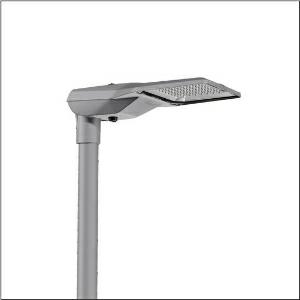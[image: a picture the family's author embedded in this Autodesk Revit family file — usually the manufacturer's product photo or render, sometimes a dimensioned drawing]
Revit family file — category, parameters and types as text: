
# Revit family: streetlight_sl_21_midi___pc-r_5xe3g33t08mb_dbe8
name_source: partatom
category: Lighting Fixtures
units: mm (PartAtom-declared; Revit-internal decimal feet)

## family parameters
Cut with Voids When Loaded = No
Host = Face
Light Source = No
Part Type = Normal
Room Calculation Point = No
Round Connector Dimension = Use Diameter
Shared = No

## types (1)
- --- (1 x LED, 17390 lm, 136 W, 3000K)
    Apparent Load = 136 VA
    CIE Flux Codes = 38 78 98 100 100
    Color Rendering = 70
    Color Temperature = 3000K
    Default Elevation = 1800 mm
    Description = Streetlight SL 21 midi, mast luminaire, primary light control with lens, of PMMA, primary optical cover: cover, of toughened safety glass, transparent, light distribution: PC-R, light emission: direct distribution, primary light characteristic: asymmetric, right, installation type: side-entry, post-top, LED, High Power LED, rated luminous flux: 17.390lm, luminous efficacy: 128lm/W, light colour: 730, colour temperature: 3000K, control gear: D4i, control: overheat protection, constant luminous flux control, time-dependent luminous flux control, flexible luminous flux parameterisation, pre-setting: logarithmic dimming characteristic, mains connection: 230..240V, AC, 50/60Hz, start of lifetime: 136W, end of service life: 142W, reduction: 61W, luminaire housing, of diecast aluminium, powder-coated, SITECO metallic grey (DB 702S), corrosivity category C5 high according to DIN EN ISO 12944, please order mast flange separately, inclination adjustable: 0°, 5°, 10°, 15°, sealing non-destructively replaceable, multi-level sealing system, length: 644mm, width: 335mm, height: 110mm, mast flange for spigot size: 42mm (side-entry): 5XC10008XM4, 60/48mm (side-entry/post-top): 5XC10108XM2, 76/60mm (side-entry/post-top): 5XC10108XM1, mounting height: 4..8m, Smart Interface below and above, protection rating (complete): IP66, insulation class (complete): insulation class II (safety insulation), certification: CE, ENEC, ENEC+, VDE, impact resistance: IK10, permissible operating ambient temperature for outdoor applications: -40..+50°C, standard-compliant lighting for roads and squares, packaging unit: 1 piece

Light Distribution: PC-R
    Height = 111 mm
    Lamp = 1 x LED
    Lamp Light Flux = 17390 lm
    Lamp Power = 136 W
    Lamp count = 1
    Length = 644 mm
    Luminous efficacy = 128 lm/W
    Manufacturer = Siteco
    ModVariant = No
    Model = 5XE3G33T08MB
    Number of Poles = 1
    OnlyDefault = Yes
    Power Factor = 1
    Product Name = Streetlight SL 21 midi | PC-R
    Product group = mast luminaire | pylon top
    ProductGroupID = 6100
    Protection Class = Protection class II
    Protection Degree = IP 66
    RLX_Detail_Level = 1
    RLX_Emergency_Light_Flux = 0 lm
    RLX_Emergency_Type = 0
    RLX_Emergency_Type_DB = No
    RlxData = <blob elided: 29501 chars, md5=56df93c5>
    Socket = socket
    Standby Power = 0 W
    System Light Flux = 17390 lm
    System Power = 136 W
    Type Comments = factory setting: luminous flux: 100 % | dim-lin: 254 | 695 mA
    Type Image = l_1004304.jpg
    URL = http://relux.com
    VarID = @adj_071813
    Voltage = 0 V
    Weight = 0.00 kg
    Width = 336 mm

## geometry (parser evidence)
native form markers: Blend x4, Sweep x12
no freeform markers — native parametric forms only
